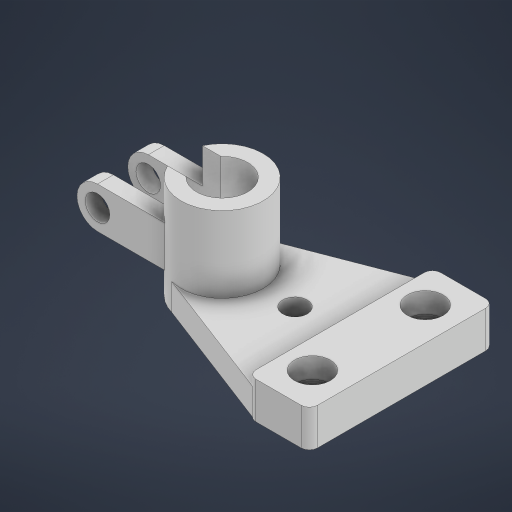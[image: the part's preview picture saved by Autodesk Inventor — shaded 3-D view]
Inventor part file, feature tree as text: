
AUTODESK INVENTOR PART (.ipt)
format: ipt  version: 2023 (Build 270158000, 158)  size: 320,000 bytes
history: native  units: mm
features: sketch x10, extrude x5, other x3, hole x3
ambient origin geometry x8: Origin, YZ Plane, XZ Plane, XY Plane, X Axis, Y Axis, Z Axis, Center Point
bodies: Body1 (feature_tree)
feature tree (21):
  other  "Bryła1"
  extrude  "Wyciągnięcie proste1"  Depth=60.0mm
  extrude  "Wyciągnięcie proste2"  Depth=180.0mm
  extrude  "Wyciągnięcie proste3"  Depth=8.0mm
  extrude  "Wyciągnięcie proste4"  Depth=3.665191mm
  extrude  "Wyciągnięcie proste5"  Depth=3.665191mm
  sketch  "Szkic6"
  sketch  "Szkic7"
  hole  "Otwór1"  [1 undecoded]
  hole  "Otwór2"  [1 undecoded]
  sketch  "Szkic9"
  hole  "Otwór3"  [1 undecoded]
  other  "Zaokrąglenie pełne1"
  other  "Zaokrąglenie pełne2"
  sketch  "Szkic1"
  sketch  "Szkic2"
  sketch  "Szkic3"
  sketch  "Szkic4"
  sketch  "Szkic5"
  sketch  "Szkic8"
  sketch  "Szkic10"
note: 3 required parameter values undecoded (feature->parameter linkage not recoverable at this tier; creation-order binding heuristic only, values carry confidence <= 0.55)
